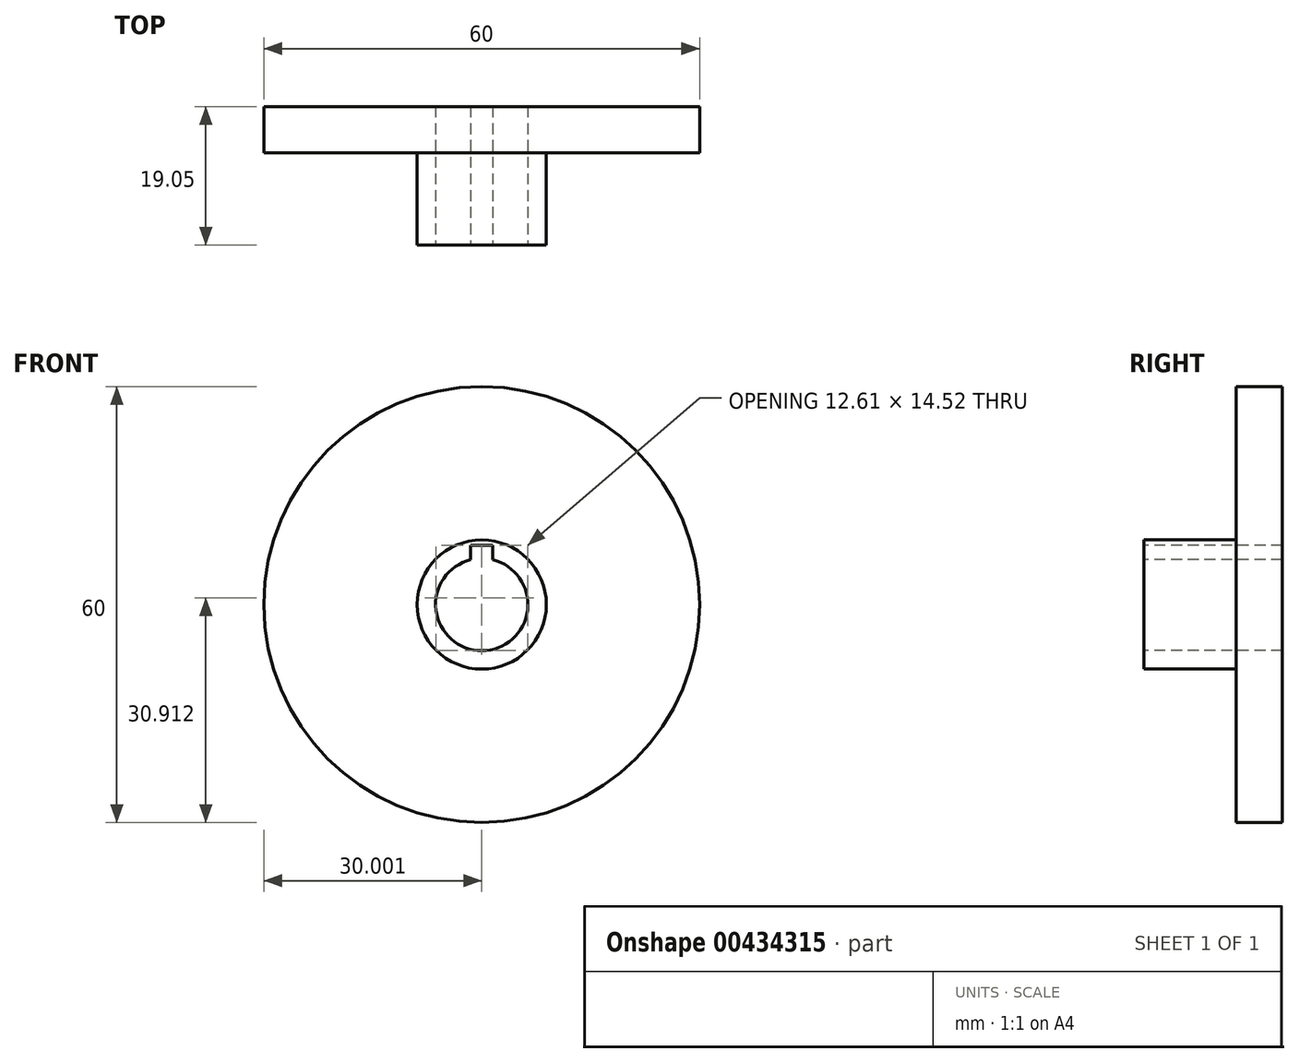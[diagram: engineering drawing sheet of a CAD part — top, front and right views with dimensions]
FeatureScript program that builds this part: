
annotation { "Feature Type Name" : "Feature", "Feature Type Description" : "" }
export const myFeature = defineFeature(function(context is Context, id is Id, definition is map)
    precondition{}
    {
        {
            var Q0;
            Q0=qCreatedBy(makeId("Front.planeOp"),FACE);
            var sketch = newSketch(context, id + "F0", { "sketchPlane" : qUnion([Q0])});
            skCircle(sketch, "E0", {"center": v(0, 0) * mm, "radius": 30 * mm});
            skSolve(sketch);
        }
        {
            var Q0;
            Q0=makeQuery(id+"F0.imprint","IMPRINT",FACE,{"disambiguationData":[TD([[makeQuery(id+"F0.imprint","IMPRINT",EDGE,{"derivedFrom":sQuery(id+"F0.wireOp",EDGE,"E0")}),1.0]])]});
            extrude(context, id + "F1", {"entities" : qUnion([Q0]), "depth" : 6.35 * mm});
        }
        {
            var Q0;
            Q0=makeQuery(id+"F1.opExtrude","CAP_FACE",FACE,{"disambiguationData":[OSD([sQuery(id+"F0.wireOp",EDGE,"E0")])],"isStart":false});
            var sketch = newSketch(context, id + "F2", { "sketchPlane" : qUnion([Q0])});
            skCircle(sketch, "E1", {"center": v(0, 0) * mm, "radius": 6.35 * mm});
            skSolve(sketch);
        }
        {
            var Q0;
            Q0=sQuery(id+"F2.wireOp",VERTEX,"E1.center");
            var Q1;
            Q1=makeQuery(id+"F1.opExtrude","SWEPT_BODY",BODY,{"disambiguationData":[OSD([sQuery(id+"F0.wireOp",EDGE,"E0")])]});
            hole(context, id + "F3", {"style" : HoleStyle.SIMPLE, "endStyle" : HoleEndStyle.THROUGH, "holeDiameter" : 12.7 * mm, "isTappedThrough" : true, "tappedDepth" : 12.7 * mm, "tapClearance" : 3, "locations" : qUnion([Q0]), "scope" : qUnion([Q1])});
        }
        {
            var Q0;
            Q0=makeQuery(id+"F1.opExtrude","CAP_FACE",FACE,{"disambiguationData":[OSD([sQuery(id+"F0.wireOp",EDGE,"E0")])],"isStart":false});
            var sketch = newSketch(context, id + "F4", { "sketchPlane" : qUnion([Q0])});
            skCircle(sketch, "E2", {"center": v(0, 0) * mm, "radius": 8.9 * mm});
            skSolve(sketch);
        }
        {
            var Q0;
            Q0=makeQuery(id+"F4.imprint","IMPRINT",FACE,{"disambiguationData":[TD([[makeQuery(id+"F4.imprint","IMPRINT",EDGE,{"derivedFrom":sQuery(id+"F4.wireOp",EDGE,"E2")}),1.0]])]});
            extrude(context, id + "F5", {"entities" : qUnion([Q0]), "operationType" : NewBodyOperationType.ADD, "depth" : 12.7 * mm});
        }
        {
            var Q0;
            Q0=makeQuery(id+"F5.opExtrude","CAP_FACE",FACE,{"disambiguationData":[OSD([sQuery(id+"F3.hole-0.sketch.wireOp",EDGE,"core_line_2"),sQuery(id+"F3.hole-0.sketch.wireOp",EDGE,"core_line_3"),sQuery(id+"F4.wireOp",EDGE,"E2")])],"isStart":false});
            var sketch = newSketch(context, id + "F6", { "sketchPlane" : qUnion([Q0])});
            skLineSegment(sketch, "E3", {"start": v(-1.51, 6.17) * mm, "end": v(-1.51, 8.17) * mm});
            skLineSegment(sketch, "E4", {"start": v(-1.51, 8.17) * mm, "end": v(1.49, 8.17) * mm});
            skLineSegment(sketch, "E5", {"start": v(1.49, 8.17) * mm, "end": v(1.49, 6.17) * mm});
            skSolve(sketch);
        }
        {
            var Q0;
            {var subQ0=sQuery(id+"F6.wireOp",EDGE,"E3");Q0=makeQuery(id+"F6.imprint","IMPRINT",FACE,{"disambiguationData":[TD([[makeQuery(id+"F6.imprint","IMPRINT",EDGE,{"derivedFrom":subQ0}),-1.0]])]});}
            extrude(context, id + "F7", {"entities" : qUnion([Q0]), "operationType" : NewBodyOperationType.REMOVE, "oppositeDirection" : true, "depth" : 37.34 * mm});
        }
    });
